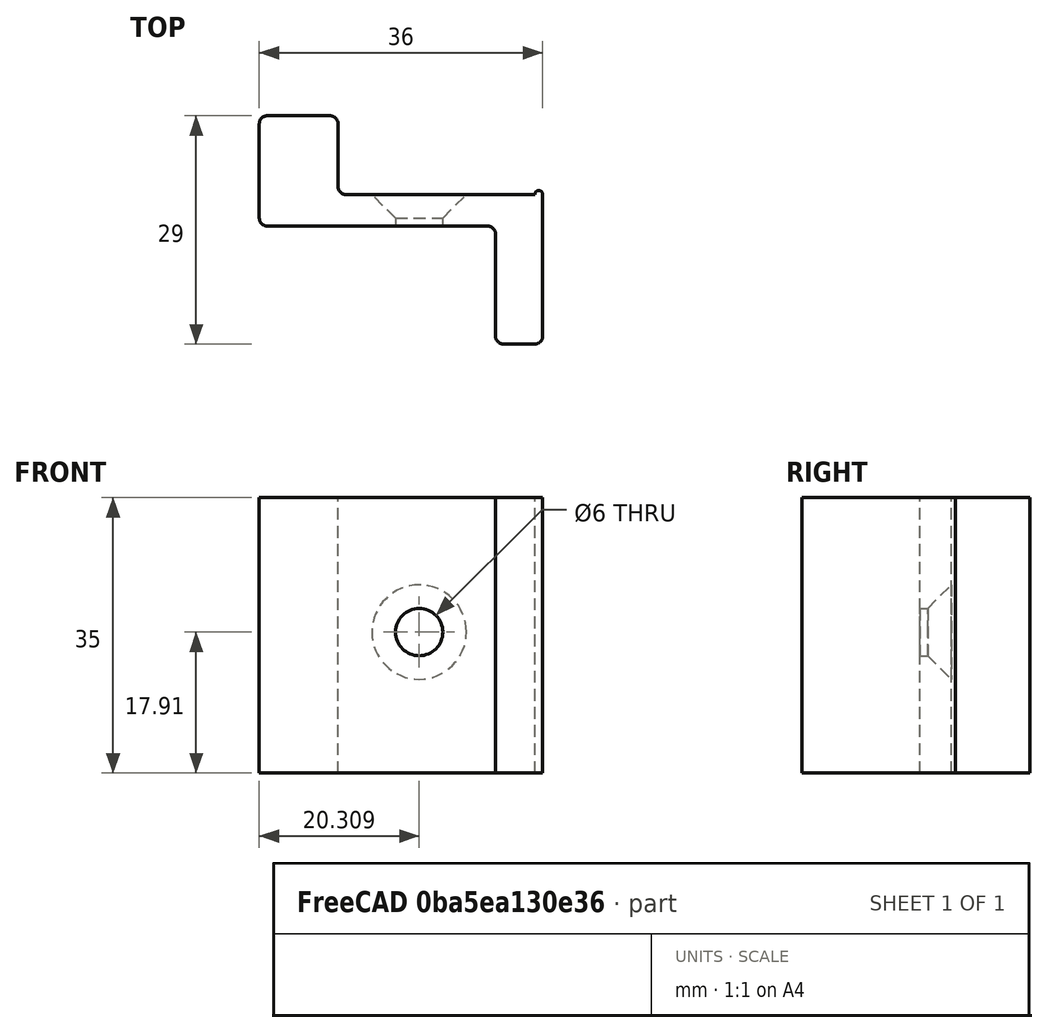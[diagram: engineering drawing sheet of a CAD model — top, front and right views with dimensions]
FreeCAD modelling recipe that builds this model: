
FCSTD DOCUMENT  (FreeCAD 0.19R)
Label: FurnaceStopper2
License: All rights reserved
LicenseURL: http://en.wikipedia.org/wiki/All_rights_reserved
objects: Sketcher::SketchObject×3, PartDesign::Pad×2, PartDesign::Pocket×1, PartDesign::Chamfer×1, PartDesign::Fillet×1, PartDesign::Body×1, Mesh::Feature×1
note: 14 computed .brp shape members not serialized (recipe doc carries the construction recipe); baked Part::Feature solids carry a one-line shape summary decoded from their .brp

FEATURE [Sketcher::SketchObject] Sketch
  FullyConstrained = true
  MapMode = 5
  Support = -> [XY_Plane]
  sketch-geometry (8):
    g0: LineSegment StartX=0 StartY=0 StartZ=0 EndX=30 EndY=0 EndZ=0
    g1: LineSegment StartX=30 StartY=0 StartZ=0 EndX=30 EndY=-15 EndZ=0
    g2: LineSegment StartX=30 StartY=-15 StartZ=0 EndX=36 EndY=-15 EndZ=0
    g3: LineSegment StartX=36 StartY=-15 StartZ=0 EndX=36 EndY=4 EndZ=0
    g4: LineSegment StartX=36 StartY=4 StartZ=0 EndX=10 EndY=4 EndZ=0
    g5: LineSegment StartX=10 StartY=4 StartZ=0 EndX=10 EndY=14 EndZ=0
    g6: LineSegment StartX=10 StartY=14 StartZ=0 EndX=0 EndY=14 EndZ=0
    g7: LineSegment StartX=0 StartY=14 StartZ=0 EndX=0 EndY=0 EndZ=0
  constraints (23):
    c: Coincident(g-1,g0)
    c: PointOnObject(g0,g-1)
    c: Coincident(g0,g1)
    c: Vertical(g1)
    c: Coincident(g1,g2)
    c: Coincident(g2,g3)
    c: Vertical(g3)
    c: Coincident(g3,g4)
    c: Horizontal(g4)
    c: Distance(g2) = 6
    c: Horizontal(g2)
    c: DistanceY(g1,g1) = 15
    c: Distance(g4) = 26
    c: Coincident(g4,g5)
    c: Coincident(g5,g6)
    c: PointOnObject(g6,g-2)
    c: Horizontal(g6)
    c: Coincident(g6,g7)
    c: Coincident(g7,g0)
    c: Vertical(g5)
    c: Distance(g6) = 10
    c: Distance(g5) = 10
    c: DistanceY(g3) = 4
FEATURE [PartDesign::Pad] Pad
  Direction = (1,1,1)
  Length = 35
  Length2 = 100
  Profile = -> Sketch
  Type = 0
FEATURE [Sketcher::SketchObject] Sketch001
  ExternalGeometry = -> [Pad]
  FullyConstrained = true
  MapMode = 5
  Placement = pos=(0,0,35) rot=(0,0,1;0rad)
  Support = -> [Pad]
  sketch-geometry (1):
    g0: Circle CenterX=35.5 CenterY=4 CenterZ=0 NormalX=0 NormalY=0 NormalZ=1 AngleXU=0 Radius=0.5
  constraints (3):
    c: Diameter(g0) = 1
    c: PointOnObject(g0,g-3)
    c: Tangent(g0,g-4)
FEATURE [PartDesign::Pad] Pad001
  BaseFeature = -> Pad
  Direction = (1,1,1)
  Length = 35
  Length2 = 100
  Profile = -> Sketch001
  Reversed = true
  Type = 0
FEATURE [Sketcher::SketchObject] Sketch002
  FullyConstrained = false
  MapMode = 5
  Placement = pos=(0,4,0) rot=(0,0.707107,0.707107;3.14159rad)
  Support = -> [Pad001]
  sketch-geometry (1):
    g0: Circle CenterX=-20.3094 CenterY=17.9104 CenterZ=0 NormalX=0 NormalY=0 NormalZ=1 AngleXU=0 Radius=3
  constraints (1):
    c: Diameter(g0) = 6
FEATURE [PartDesign::Pocket] Pocket
  BaseFeature = -> Pad001
  Length = 5
  Length2 = 100
  Profile = -> Sketch002
  Type = 1
FEATURE [PartDesign::Chamfer] Chamfer
  Angle = 45
  Base = -> Pocket [Edge24]
  BaseFeature = -> Pocket
  ChamferType = 0
  FlipDirection = false
  Size = 3
  Size2 = 1
  SupportTransform = false
FEATURE [PartDesign::Fillet] Fillet
  Base = -> Chamfer [Edge14,Edge6,Edge9,Edge29,Edge35,Edge12,Edge33]
  BaseFeature = -> Chamfer
  Radius = 1
  SupportTransform = false
FEATURE [PartDesign::Body] Body
  Group = -> [Sketch,Pad,Sketch001,Pad001,Sketch002,Pocket,Chamfer,Fillet]
  Origin = -> Origin
  Tip = -> Fillet
FEATURE [Mesh::Feature] Mesh  label="Fillet (Meshed)"
